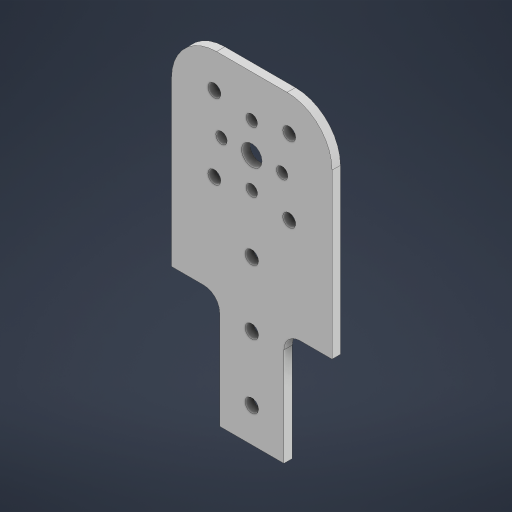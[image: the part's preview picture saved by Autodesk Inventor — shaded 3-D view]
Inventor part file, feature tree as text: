
AUTODESK INVENTOR PART (.ipt)
format: ipt  version: 2024 (Build 280153000, 153)  size: 247,808 bytes
history: native  units: in
note: dims shown in document units (in); Inventor stores cm internally (conversion verified against a paired STEP export)
features: fillet x3, sketch x3, hole x2, pattern_circular x2, extrude x1
ambient origin geometry x8: Origin, YZ Plane, XZ Plane, XY Plane, X Axis, Y Axis, Z Axis, Center Point
bodies: Solid1 (feature_tree)
feature tree (11):
  extrude  "Extrusion1"  Depth=2.5in
  fillet  "Fillet11"  Radius=0.209in
  fillet  "Fillet12"  Radius=1.125in
  hole  "Hole1"  [1 undecoded]
  pattern_circular  "Circular Pattern1"  [2 undecoded]
  hole  "Hole2"  [1 undecoded]
  pattern_circular  "Circular Pattern2"  [2 undecoded]
  fillet  "Fillet15"  [1 undecoded]
  sketch  "Sketch1"  dims[d0=2.5in d2=0.3189in d3=0.209in d5=1.125in]
  sketch  "Sketch3"  dims[d10=0.13in d11=0.0in d22=0.7in]
  sketch  "Sketch4"  dims[d23=0.7in d26=1.2598in d27=0.6299in d28=0.9449in d29=0.177in d30=0.75in d31=0.37in d32=0.25in d33=90.0deg d34=0.559in d35=0.8108in d36=90.0deg d37=1.5748in d38=360.0deg d40=0.9449in d41=1.2598in d42=1.65in d43=0.201in d44=0.432in d45=0.385in d46=0.25in d47=0.5635in d48=0.64in d49=0.8108in d50=3.25in d51=1.5748in d52=360.0deg d54=0.209in d55=2.5in d58=45.0deg d59=1.0in d60=1.0in d61=1.0in d62=0.25in d16=0.0in d17=0.0in d18=0.0in d19=0.0in d20=0.0in d21=0.0in]
note: 7 required parameter values undecoded (feature->parameter linkage not recoverable at this tier; creation-order binding heuristic only, values carry confidence <= 0.55)
